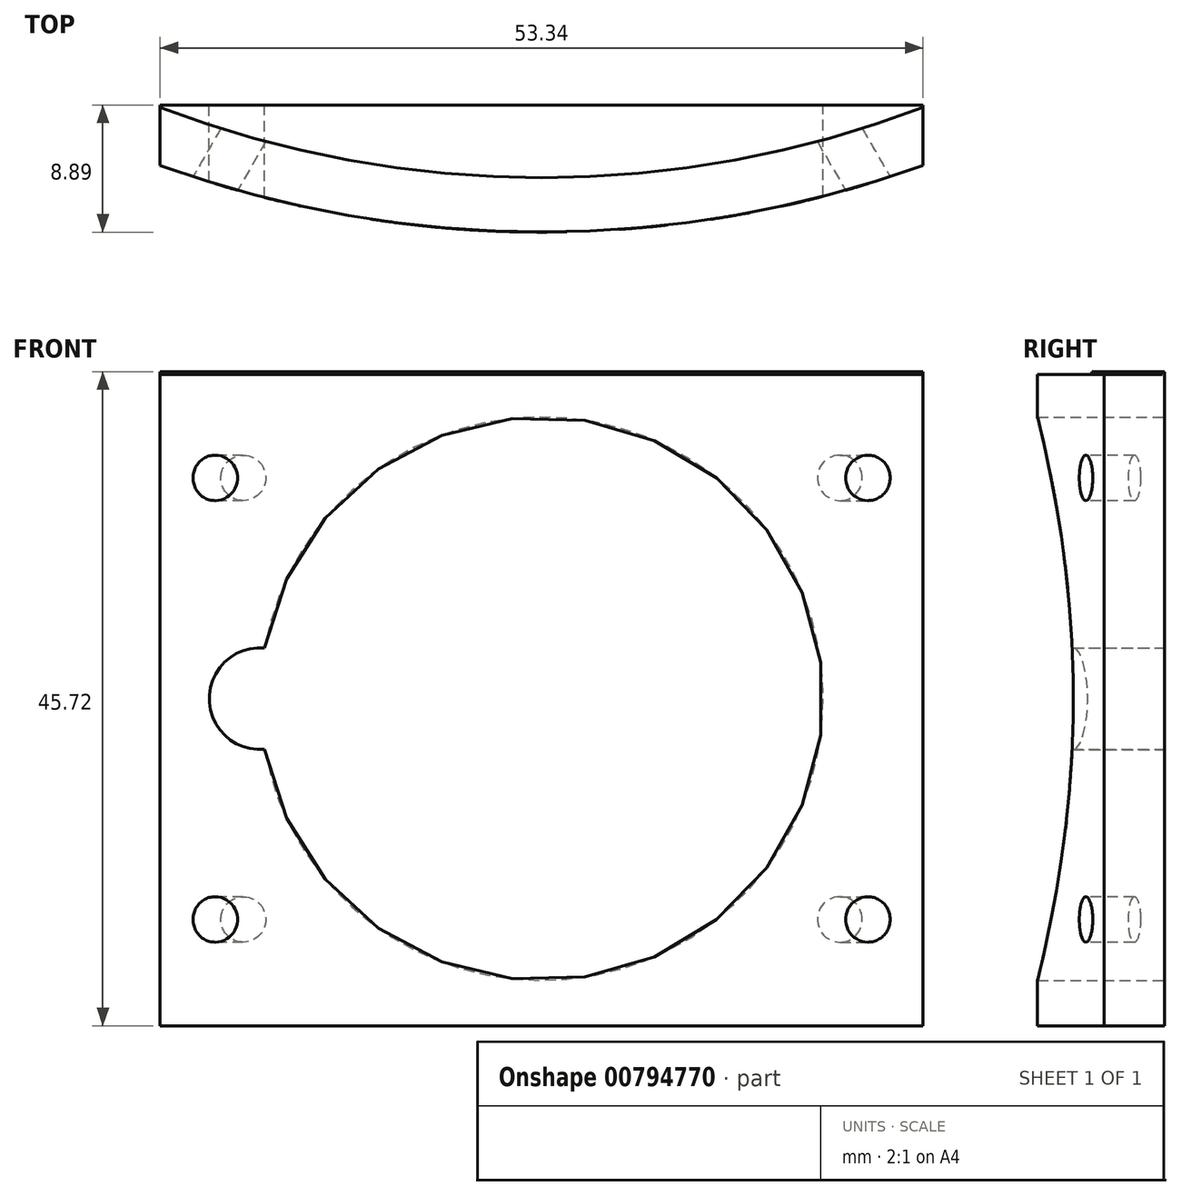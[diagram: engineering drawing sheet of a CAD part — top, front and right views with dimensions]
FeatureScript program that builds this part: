
annotation { "Feature Type Name" : "Feature", "Feature Type Description" : "" }
export const myFeature = defineFeature(function(context is Context, id is Id, definition is map)
    precondition{}
    {
        {
            var Q0;
            Q0=qCreatedBy(makeId("Top.planeOp"),FACE);
            var sketch = newSketch(context, id + "F0", { "sketchPlane" : qUnion([Q0])});
            skCircle(sketch, "E0", {"center": v(0, 0) * mm, "radius": 78.74 * mm});
            skCircle(sketch, "E1", {"center": v(0, 0) * mm, "radius": 74.93 * mm});
            skSolve(sketch);
        }
        {
            var Q0;
            Q0=makeQuery(id+"F0.imprint","IMPRINT",FACE,{"disambiguationData":[TD([[makeQuery(id+"F0.imprint","IMPRINT",EDGE,{"derivedFrom":sQuery(id+"F0.wireOp",EDGE,"E0")}),1.0]])]});
            extrude(context, id + "F1", {"entities" : qUnion([Q0]), "endBound" : BoundingType.SYMMETRIC, "depth" : 76.2 * mm, "offsetDistance" : 25.4 * mm});
        }
        {
            var Q0;
            Q0=qCreatedBy(makeId("Front.planeOp"),FACE);
            var sketch = newSketch(context, id + "F2", { "sketchPlane" : qUnion([Q0])});
            skLineSegment(sketch, "E2", {"start": v(23.81, 0) * mm, "end": v(23.81, 30.86) * mm, "construction": true});
            skCircle(sketch, "E3", {"center": v(23.81, 30.86) * mm, "radius": 1.59 * mm});
            skCircle(sketch, "E4", {"center": v(23.81, 0) * mm, "radius": 1.59 * mm});
            skLineSegment(sketch, "E5", {"start": v(0, 0) * mm, "end": v(0, 29.69) * mm, "construction": true});
            skLineSegment(sketch, "E6", {"start": v(23.81, 15.43) * mm, "end": v(0, 15.43) * mm, "construction": true});
            skCircle(sketch, "E7", {"center": v(0, 15.43) * mm, "radius": 19.69 * mm});
            skCircle(sketch, "E8.MirrorC", {"center": v(-23.81, 30.86) * mm, "radius": 1.59 * mm});
            skCircle(sketch, "E9.MirrorC", {"center": v(-23.81, 0) * mm, "radius": 1.59 * mm});
            skLineSegment(sketch, "E10.bottom", {"start": v(0, 15.43) * mm, "end": v(26.67, 15.43) * mm});
            skLineSegment(sketch, "E10.top", {"start": v(0, 38.3) * mm, "end": v(26.67, 38.3) * mm});
            skLineSegment(sketch, "E10.left", {"start": v(0, 15.43) * mm, "end": v(0, 38.3) * mm});
            skLineSegment(sketch, "E10.right", {"start": v(26.67, 15.43) * mm, "end": v(26.67, 38.3) * mm});
            skLineSegment(sketch, "E11.MirrorCS", {"start": v(26.67, 15.43) * mm, "end": v(26.67, -7.43) * mm});
            skLineSegment(sketch, "E12.MirrorCS", {"start": v(0, -7.43) * mm, "end": v(26.67, -7.43) * mm});
            skLineSegment(sketch, "E13.MirrorCS", {"start": v(0, 15.43) * mm, "end": v(0, -7.43) * mm});
            skLineSegment(sketch, "E14.MirrorCS", {"start": v(0, 38.3) * mm, "end": v(-26.67, 38.3) * mm});
            skLineSegment(sketch, "E15.MirrorCS", {"start": v(-26.67, 15.43) * mm, "end": v(-26.67, 38.3) * mm});
            skLineSegment(sketch, "E16.MirrorCS", {"start": v(0, 15.43) * mm, "end": v(-26.67, 15.43) * mm});
            skLineSegment(sketch, "E17.MirrorCS", {"start": v(-26.67, 15.43) * mm, "end": v(-26.67, -7.43) * mm});
            skLineSegment(sketch, "E18.MirrorCS", {"start": v(0, -7.43) * mm, "end": v(-26.67, -7.43) * mm});
            skSolve(sketch);
        }
        {
            var Q0;
            Q0=makeQuery(id+"F2.imprint","IMPRINT",FACE,{"disambiguationData":[TD([[makeQuery(id+"F2.imprint","IMPRINT",EDGE,{"derivedFrom":sQuery(id+"F2.wireOp",EDGE,"E8.MirrorC")}),1.0]])]});
            var Q1;
            Q1=makeQuery(id+"F2.imprint","IMPRINT",FACE,{"disambiguationData":[TD([[makeQuery(id+"F2.imprint","IMPRINT",EDGE,{"derivedFrom":sQuery(id+"F2.wireOp",EDGE,"E9.MirrorC")}),1.0]])]});
            var Q2;
            Q2=makeQuery(id+"F2.imprint","IMPRINT",FACE,{"disambiguationData":[TD([[makeQuery(id+"F2.imprint","IMPRINT",EDGE,{"derivedFrom":sQuery(id+"F2.wireOp",EDGE,"E4")}),-1.0]])]});
            var Q3;
            Q3=makeQuery(id+"F2.imprint","IMPRINT",FACE,{"disambiguationData":[TD([[makeQuery(id+"F2.imprint","IMPRINT",EDGE,{"derivedFrom":sQuery(id+"F2.wireOp",EDGE,"E3")}),-1.0]])]});
            var Q4;
            Q4=makeQuery(id+"F2.imprint","IMPRINT",FACE,{"disambiguationData":[TD([[makeQuery(id+"F2.imprint","IMPRINT",EDGE,{"derivedFrom":sQuery(id+"F2.wireOp",EDGE,"E8.MirrorC")}),-1.0]])]});
            var Q5;
            Q5=makeQuery(id+"F2.imprint","IMPRINT",FACE,{"disambiguationData":[TD([[makeQuery(id+"F2.imprint","IMPRINT",EDGE,{"derivedFrom":sQuery(id+"F2.wireOp",EDGE,"E3")}),1.0]])]});
            var Q6;
            Q6=makeQuery(id+"F2.imprint","IMPRINT",FACE,{"disambiguationData":[TD([[makeQuery(id+"F2.imprint","IMPRINT",EDGE,{"derivedFrom":sQuery(id+"F2.wireOp",EDGE,"E9.MirrorC")}),-1.0]])]});
            var Q7;
            Q7=makeQuery(id+"F2.imprint","IMPRINT",FACE,{"disambiguationData":[TD([[makeQuery(id+"F2.imprint","IMPRINT",EDGE,{"derivedFrom":sQuery(id+"F2.wireOp",EDGE,"E4")}),1.0]])]});
            extrude(context, id + "F3", {"entities" : qUnion([Q0, Q1, Q2, Q3, Q4, Q5, Q6, Q7]), "operationType" : NewBodyOperationType.INTERSECT, "depth" : 177.8 * mm, "offsetDistance" : 25.4 * mm});
        }
        {
            var Q0;
            Q0=makeQuery(id+"F1.opExtrude","CAP_FACE",FACE,{"disambiguationData":[OSD([sQuery(id+"F0.wireOp",EDGE,"E0"),sQuery(id+"F0.wireOp",EDGE,"E1")])],"isStart":false});
            var sketch = newSketch(context, id + "F4", { "sketchPlane" : qUnion([Q0])});
            skLineSegment(sketch, "E19", {"start": v(26.67, -74.09) * mm, "end": v(14.63, -81.04) * mm});
            skLineSegment(sketch, "E20", {"start": v(26.67, -74.09) * mm, "end": v(-26.67, -74.09) * mm, "construction": true});
            skSolve(sketch);
        }
        {
            var Q0;
            Q0=sQuery(id+"F4.wireOp",EDGE,"E19");
            extrude(context, id + "F5", {"bodyType" : ToolBodyType.SURFACE, "surfaceEntities" : qUnion([Q0]), "depth" : 0.03 * mm, "offsetDistance" : 25.4 * mm});
        }
        {
            var Q0;
            Q0=makeQuery(id+"F5.opExtrude","SWEPT_FACE",FACE,{"disambiguationData":[OSD([sQuery(id+"F4.wireOp",EDGE,"E19")])]});
            var sketch = newSketch(context, id + "F6", { "sketchPlane" : qUnion([Q0])});
            skLineSegment(sketch, "E21.0", {"start": v(13.95, 38.1) * mm, "end": v(13.95, -7.43) * mm});
            skLineSegment(sketch, "E22", {"start": v(17.92, 38.1) * mm, "end": v(17.92, -7.4) * mm});
            skPoint(sketch, "E23", {"position": v(17.92, 30.86) * mm});
            skPoint(sketch, "E24", {"position": v(17.92, 0) * mm});
            skCircle(sketch, "E25", {"center": v(17.92, 30.86) * mm, "radius": 1.59 * mm});
            skCircle(sketch, "E26", {"center": v(17.92, 0) * mm, "radius": 1.59 * mm});
            skSolve(sketch);
        }
        {
            var Q0;
            {var subQ0=sQuery(id+"F6.wireOp",EDGE,"E26");var subQ1=sQuery(id+"F6.wireOp",EDGE,"E22");var subQ2=makeQuery(id+"F6.imprint","INTERSECT",VERTEX,{"disambiguationData":[OD(0.0)],"derivedFrom":[subQ1,subQ0]});Q0=makeQuery(id+"F6.imprint","IMPRINT",FACE,{"disambiguationData":[TD([[makeQuery(id+"F6.imprint","IMPRINT",EDGE,{"disambiguationData":[TD([[subQ2,1.0]])],"derivedFrom":subQ1}),1.0]])]});}
            var Q1;
            {var subQ0=sQuery(id+"F6.wireOp",EDGE,"E26");var subQ1=sQuery(id+"F6.wireOp",EDGE,"E22");var subQ2=makeQuery(id+"F6.imprint","INTERSECT",VERTEX,{"disambiguationData":[OD(0.0)],"derivedFrom":[subQ1,subQ0]});Q1=makeQuery(id+"F6.imprint","IMPRINT",FACE,{"disambiguationData":[TD([[makeQuery(id+"F6.imprint","IMPRINT",EDGE,{"disambiguationData":[TD([[subQ2,1.0]])],"derivedFrom":subQ1}),-1.0]])]});}
            var Q2;
            {var subQ0=sQuery(id+"F6.wireOp",EDGE,"E25");var subQ1=sQuery(id+"F6.wireOp",EDGE,"E22");var subQ2=makeQuery(id+"F6.imprint","INTERSECT",VERTEX,{"disambiguationData":[OD(0.0)],"derivedFrom":[subQ1,subQ0]});Q2=makeQuery(id+"F6.imprint","IMPRINT",FACE,{"disambiguationData":[TD([[makeQuery(id+"F6.imprint","IMPRINT",EDGE,{"disambiguationData":[TD([[subQ2,1.0]])],"derivedFrom":subQ1}),-1.0]])]});}
            var Q3;
            {var subQ0=sQuery(id+"F6.wireOp",EDGE,"E25");var subQ1=sQuery(id+"F6.wireOp",EDGE,"E22");var subQ2=makeQuery(id+"F6.imprint","INTERSECT",VERTEX,{"disambiguationData":[OD(0.0)],"derivedFrom":[subQ1,subQ0]});Q3=makeQuery(id+"F6.imprint","IMPRINT",FACE,{"disambiguationData":[TD([[makeQuery(id+"F6.imprint","IMPRINT",EDGE,{"disambiguationData":[TD([[subQ2,1.0]])],"derivedFrom":subQ1}),1.0]])]});}
            extrude(context, id + "F7", {"entities" : qUnion([Q0, Q1, Q2, Q3]), "operationType" : NewBodyOperationType.REMOVE, "depth" : 25.4 * mm, "offsetDistance" : 25.4 * mm});
        }
        {
            var Q0;
            Q0=qCreatedBy(makeId("Right.planeOp"),FACE);
            var sketch = newSketch(context, id + "F8", { "sketchPlane" : qUnion([Q0])});
            skLineSegment(sketch, "E27.bottom", {"start": v(22.44, 106.55) * mm, "end": v(-147.71, 106.55) * mm});
            skLineSegment(sketch, "E27.top", {"start": v(22.44, -70.52) * mm, "end": v(-147.71, -70.52) * mm});
            skLineSegment(sketch, "E27.left", {"start": v(22.44, 106.55) * mm, "end": v(22.44, -70.52) * mm});
            skLineSegment(sketch, "E27.right", {"start": v(-147.71, 106.55) * mm, "end": v(-147.71, -70.52) * mm});
            skSolve(sketch);
        }
        {
            var Q0;
            Q0=makeQuery(id+"F8.imprint","IMPRINT",FACE,{"disambiguationData":[TD([[makeQuery(id+"F8.imprint","IMPRINT",EDGE,{"derivedFrom":sQuery(id+"F8.wireOp",EDGE,"E27.bottom")}),1.0]])]});
            extrude(context, id + "F9", {"entities" : qUnion([Q0]), "operationType" : NewBodyOperationType.REMOVE, "oppositeDirection" : true, "depth" : 76.2 * mm, "offsetDistance" : 25.4 * mm});
        }
        {
            var Q0;
            Q0=makeQuery(id+"F1.opExtrude","SWEPT_BODY",BODY,{"disambiguationData":[OSD([sQuery(id+"F0.wireOp",EDGE,"E0"),sQuery(id+"F0.wireOp",EDGE,"E1")])]});
            var Q1;
            Q1=qCreatedBy(makeId("Right.planeOp"),FACE);
            mirror(context, id + "F10", {"operationType" : NewBodyOperationType.ADD, "entities" : qUnion([Q0]), "mirrorPlane" : qUnion([Q1])});
        }
        {
            var Q0;
            {var subQ0=makeQuery(id+"F1.opExtrude","CAP_FACE",FACE,{"disambiguationData":[OSD([sQuery(id+"F0.wireOp",EDGE,"E0"),sQuery(id+"F0.wireOp",EDGE,"E1")])],"isStart":false});Q0=makeQuery(id+"F10.boolean.opBoolean","MERGE",FACE,{"derivedFrom":[subQ0,makeQuery(id+"F10.opPattern","COPY",FACE,{"derivedFrom":subQ0,"instanceName":"1"})]});}
            var sketch = newSketch(context, id + "F11", { "sketchPlane" : qUnion([Q0])});
            skLineSegment(sketch, "E28", {"start": v(-26.67, -70.02) * mm, "end": v(26.67, -70.02) * mm});
            skSolve(sketch);
        }
        {
            var Q0;
            Q0=makeQuery(id+"F2.imprint","IMPRINT",FACE,{"disambiguationData":[TD([[makeQuery(id+"F2.imprint","IMPRINT",EDGE,{"derivedFrom":sQuery(id+"F2.wireOp",EDGE,"E3")}),-1.0]])]});
            var Q1;
            Q1=makeQuery(id+"F2.imprint","IMPRINT",FACE,{"disambiguationData":[TD([[makeQuery(id+"F2.imprint","IMPRINT",EDGE,{"derivedFrom":sQuery(id+"F2.wireOp",EDGE,"E8.MirrorC")}),1.0]])]});
            var Q2;
            Q2=makeQuery(id+"F2.imprint","IMPRINT",FACE,{"disambiguationData":[TD([[makeQuery(id+"F2.imprint","IMPRINT",EDGE,{"derivedFrom":sQuery(id+"F2.wireOp",EDGE,"E9.MirrorC")}),1.0]])]});
            var Q3;
            Q3=makeQuery(id+"F2.imprint","IMPRINT",FACE,{"disambiguationData":[TD([[makeQuery(id+"F2.imprint","IMPRINT",EDGE,{"derivedFrom":sQuery(id+"F2.wireOp",EDGE,"E4")}),-1.0]])]});
            var Q4;
            Q4=makeQuery(id+"F2.imprint","IMPRINT",FACE,{"disambiguationData":[TD([[makeQuery(id+"F2.imprint","IMPRINT",EDGE,{"derivedFrom":sQuery(id+"F2.wireOp",EDGE,"E9.MirrorC")}),-1.0]])]});
            var Q5;
            Q5=makeQuery(id+"F2.imprint","IMPRINT",FACE,{"disambiguationData":[TD([[makeQuery(id+"F2.imprint","IMPRINT",EDGE,{"derivedFrom":sQuery(id+"F2.wireOp",EDGE,"E8.MirrorC")}),-1.0]])]});
            var Q6;
            Q6=makeQuery(id+"F2.imprint","IMPRINT",FACE,{"disambiguationData":[TD([[makeQuery(id+"F2.imprint","IMPRINT",EDGE,{"derivedFrom":sQuery(id+"F2.wireOp",EDGE,"E3")}),1.0]])]});
            var Q7;
            Q7=makeQuery(id+"F2.imprint","IMPRINT",FACE,{"disambiguationData":[TD([[makeQuery(id+"F2.imprint","IMPRINT",EDGE,{"derivedFrom":sQuery(id+"F2.wireOp",EDGE,"E4")}),1.0]])]});
            var Q8;
            {var subQ0=makeQuery(id+"F1.opExtrude","SWEPT_FACE",FACE,{"disambiguationData":[OSD([sQuery(id+"F0.wireOp",EDGE,"E1")])]});Q8=makeQuery(id+"F10.boolean.opBoolean","MERGE",FACE,{"derivedFrom":[subQ0,makeQuery(id+"F10.opPattern","COPY",FACE,{"derivedFrom":subQ0,"instanceName":"1"})]});}
            extrude(context, id + "F12", {"entities" : qUnion([Q0, Q1, Q2, Q3, Q4, Q5, Q6, Q7]), "operationType" : NewBodyOperationType.ADD, "endBound" : BoundingType.UP_TO_SURFACE, "depth" : 25.4 * mm, "endBoundEntityFace" : qUnion([Q8]), "offsetDistance" : 25.4 * mm});
        }
        {
            var Q0;
            Q0=makeQuery(id+"F2.imprint","IMPRINT",FACE,{"disambiguationData":[TD([[makeQuery(id+"F2.imprint","IMPRINT",EDGE,{"derivedFrom":sQuery(id+"F2.wireOp",EDGE,"E4")}),-1.0]])]});
            var Q1;
            Q1=makeQuery(id+"F2.imprint","IMPRINT",FACE,{"disambiguationData":[TD([[makeQuery(id+"F2.imprint","IMPRINT",EDGE,{"derivedFrom":sQuery(id+"F2.wireOp",EDGE,"E8.MirrorC")}),1.0]])]});
            var Q2;
            Q2=makeQuery(id+"F2.imprint","IMPRINT",FACE,{"disambiguationData":[TD([[makeQuery(id+"F2.imprint","IMPRINT",EDGE,{"derivedFrom":sQuery(id+"F2.wireOp",EDGE,"E9.MirrorC")}),1.0]])]});
            var Q3;
            Q3=makeQuery(id+"F2.imprint","IMPRINT",FACE,{"disambiguationData":[TD([[makeQuery(id+"F2.imprint","IMPRINT",EDGE,{"derivedFrom":sQuery(id+"F2.wireOp",EDGE,"E3")}),-1.0]])]});
            var Q4;
            Q4=makeQuery(id+"F2.imprint","IMPRINT",FACE,{"disambiguationData":[TD([[makeQuery(id+"F2.imprint","IMPRINT",EDGE,{"derivedFrom":sQuery(id+"F2.wireOp",EDGE,"E9.MirrorC")}),-1.0]])]});
            var Q5;
            Q5=makeQuery(id+"F2.imprint","IMPRINT",FACE,{"disambiguationData":[TD([[makeQuery(id+"F2.imprint","IMPRINT",EDGE,{"derivedFrom":sQuery(id+"F2.wireOp",EDGE,"E4")}),1.0]])]});
            var Q6;
            Q6=makeQuery(id+"F2.imprint","IMPRINT",FACE,{"disambiguationData":[TD([[makeQuery(id+"F2.imprint","IMPRINT",EDGE,{"derivedFrom":sQuery(id+"F2.wireOp",EDGE,"E3")}),1.0]])]});
            var Q7;
            Q7=makeQuery(id+"F2.imprint","IMPRINT",FACE,{"disambiguationData":[TD([[makeQuery(id+"F2.imprint","IMPRINT",EDGE,{"derivedFrom":sQuery(id+"F2.wireOp",EDGE,"E8.MirrorC")}),-1.0]])]});
            extrude(context, id + "F13", {"entities" : qUnion([Q0, Q1, Q2, Q3, Q4, Q5, Q6, Q7]), "operationType" : NewBodyOperationType.REMOVE, "depth" : 69.85 * mm, "offsetDistance" : 25.4 * mm});
        }
        {
            var Q0;
            Q0=makeQuery(id+"F13.boolean.opBoolean","COPY",FACE,{"derivedFrom":makeQuery(id+"F13.opExtrude","CAP_FACE",FACE,{"disambiguationData":[OSD([sQuery(id+"F2.wireOp",EDGE,"E7"),sQuery(id+"F2.wireOp",EDGE,"E10.top"),sQuery(id+"F2.wireOp",EDGE,"E10.right"),sQuery(id+"F2.wireOp",EDGE,"E11.MirrorCS"),sQuery(id+"F2.wireOp",EDGE,"E12.MirrorCS"),sQuery(id+"F2.wireOp",EDGE,"E14.MirrorCS"),sQuery(id+"F2.wireOp",EDGE,"E15.MirrorCS"),sQuery(id+"F2.wireOp",EDGE,"E17.MirrorCS"),sQuery(id+"F2.wireOp",EDGE,"E18.MirrorCS")])],"isStart":false})});
            var sketch = newSketch(context, id + "F14", { "sketchPlane" : qUnion([Q0])});
            skCircle(sketch, "E29.0", {"center": v(0, 15.43) * mm, "radius": 19.69 * mm});
            skLineSegment(sketch, "E30", {"start": v(0, 15.43) * mm, "end": v(3.15, 15.43) * mm});
            skLineSegment(sketch, "E31", {"start": v(0, 15.43) * mm, "end": v(19.69, 15.43) * mm});
            skCircle(sketch, "E32", {"center": v(19.69, 15.43) * mm, "radius": 3.56 * mm});
            skSolve(sketch);
        }
        {
            var Q0;
            {var subQ0=sQuery(id+"F14.wireOp",EDGE,"E29.0");var subQ1=makeQuery(id+"F14.imprint","INTERSECT",VERTEX,{"derivedFrom":[subQ0,sQuery(id+"F14.wireOp",EDGE,"E31")]});Q0=makeQuery(id+"F14.imprint","IMPRINT",FACE,{"disambiguationData":[TD([[makeQuery(id+"F14.imprint","IMPRINT",EDGE,{"disambiguationData":[TD([[subQ1,1.0]])],"derivedFrom":subQ0}),1.0]])]});}
            extrude(context, id + "F15", {"entities" : qUnion([Q0]), "operationType" : NewBodyOperationType.REMOVE, "endBound" : BoundingType.THROUGH_ALL, "oppositeDirection" : true, "depth" : 25.4 * mm, "offsetDistance" : 25.4 * mm});
        }
    });
